FCSTD DOCUMENT  (FreeCAD 0.19R0.19.2)
Label: laptopStand015
License: All rights reserved
LicenseURL: http://en.wikipedia.org/wiki/All_rights_reserved
objects: Sketcher::SketchObject×1
note: 1 computed .brp shape members not serialized (recipe doc carries the construction recipe); baked Part::Feature solids carry a one-line shape summary decoded from their .brp

FEATURE [Sketcher::SketchObject] Sketch
  FullyConstrained = false
  sketch-geometry (54):
    g0: LineSegment StartX=-22.9272 StartY=136.221 StartZ=0 EndX=-22.9272 EndY=-103.779 EndZ=0
    g1: LineSegment StartX=-22.9272 StartY=136.221 StartZ=0 EndX=387.073 EndY=136.221 EndZ=0
    g2: LineSegment StartX=-22.9272 StartY=-103.779 StartZ=0 EndX=387.073 EndY=-103.779 EndZ=0
    g3: LineSegment StartX=387.073 StartY=136.221 StartZ=0 EndX=387.073 EndY=-103.779 EndZ=0
    g4: LineSegment StartX=-10.9272 StartY=124.221 StartZ=0 EndX=-10.9272 EndY=115.221 EndZ=0
    g5: LineSegment StartX=-10.9272 StartY=124.221 StartZ=0 EndX=-1.92719 EndY=124.221 EndZ=0
    g6: LineSegment StartX=-10.9272 StartY=-91.7794 StartZ=0 EndX=-10.9272 EndY=-82.7794 EndZ=0
    g7: LineSegment StartX=-10.9272 StartY=-91.7794 StartZ=0 EndX=-1.92719 EndY=-91.7794 EndZ=0
    g8: LineSegment StartX=375.073 StartY=-91.7794 StartZ=0 EndX=366.073 EndY=-91.7794 EndZ=0
    g9: LineSegment StartX=375.073 StartY=-91.7794 StartZ=0 EndX=375.073 EndY=-82.7794 EndZ=0
    g10: LineSegment StartX=375.073 StartY=115.221 StartZ=0 EndX=318.073 EndY=83.9235 EndZ=0
    g11: LineSegment StartX=-10.9272 StartY=-82.7794 StartZ=0 EndX=169.377 EndY=16.2206 EndZ=0
    g12: LineSegment StartX=-1.92719 StartY=124.221 StartZ=0 EndX=139.632 EndY=46.4944 EndZ=0
    g13: LineSegment StartX=366.073 StartY=-91.7794 StartZ=0 EndX=318.073 EndY=-65.424 EndZ=0
    g14: LineSegment StartX=366.073 StartY=124.221 StartZ=0 EndX=318.073 EndY=124.221 EndZ=0
    g15: LineSegment StartX=-10.9272 StartY=115.221 StartZ=0 EndX=-10.9272 EndY=-82.7794 EndZ=0
    g16: LineSegment StartX=-1.92719 StartY=-91.7794 StartZ=0 EndX=366.073 EndY=-91.7794 EndZ=0
    g17: LineSegment StartX=375.073 StartY=-82.7794 StartZ=0 EndX=375.073 EndY=115.221 EndZ=0
    g18: LineSegment StartX=-1.92719 StartY=124.221 StartZ=0 EndX=58.0728 EndY=124.221 EndZ=0
    g19: LineSegment StartX=-1.92719 StartY=-91.7794 StartZ=0 EndX=58.0728 EndY=-91.7794 EndZ=0
    g20: LineSegment StartX=306.073 StartY=-91.7794 StartZ=0 EndX=366.073 EndY=-91.7794 EndZ=0
    g21: LineSegment StartX=318.073 StartY=124.221 StartZ=0 EndX=366.073 EndY=124.221 EndZ=0
    g22: LineSegment StartX=58.0728 StartY=124.221 StartZ=0 EndX=46.0728 EndY=124.221 EndZ=0
    g23: LineSegment StartX=318.073 StartY=-91.7794 StartZ=0 EndX=306.073 EndY=-91.7794 EndZ=0
    g24: LineSegment StartX=58.0728 StartY=-91.7794 StartZ=0 EndX=46.0728 EndY=-91.7794 EndZ=0
    g25: LineSegment StartX=306.073 StartY=-81.8102 StartZ=0 EndX=224.513 EndY=-14.0532 EndZ=0
    g26: LineSegment StartX=46.0728 StartY=124.221 StartZ=0 EndX=139.632 EndY=46.4944 EndZ=0
    g27: LineSegment StartX=306.073 StartY=124.221 StartZ=0 EndX=189.124 EndY=27.0628 EndZ=0
    g28: LineSegment StartX=58.0728 StartY=-91.7794 StartZ=0 EndX=175.022 EndY=5.37834 EndZ=0
    g29: LineSegment StartX=46.0728 StartY=124.221 StartZ=0 EndX=46.0728 EndY=-91.7794 EndZ=0
    g30: LineSegment StartX=58.0728 StartY=-91.7794 StartZ=0 EndX=58.0728 EndY=124.221 EndZ=0
    g31: LineSegment StartX=318.073 StartY=124.221 StartZ=0 EndX=318.073 EndY=97.8651 EndZ=0
    g32: LineSegment StartX=306.073 StartY=114.251 StartZ=0 EndX=306.073 EndY=91.2763 EndZ=0
    g33: LineSegment StartX=182.073 StartY=23.1914 StartZ=0 EndX=189.124 EndY=27.0628 EndZ=0
    g34: LineSegment StartX=182.073 StartY=9.24976 StartZ=0 EndX=175.022 EndY=5.37834 EndZ=0
    g35: LineSegment StartX=224.513 StartY=46.4944 StartZ=0 EndX=306.073 EndY=114.251 EndZ=0
    g36: LineSegment StartX=175.022 StartY=27.0628 StartZ=0 EndX=58.0728 EndY=124.221 EndZ=0
    g37: LineSegment StartX=169.377 StartY=16.2206 StartZ=0 EndX=-10.9272 EndY=115.221 EndZ=0
    g38: LineSegment StartX=139.632 StartY=-14.0532 StartZ=0 EndX=46.0728 EndY=-91.7794 EndZ=0
    g39: LineSegment StartX=194.768 StartY=16.2206 StartZ=0 EndX=306.073 EndY=-44.8935 EndZ=0
    g40: LineSegment StartX=224.513 StartY=46.4944 StartZ=0 EndX=306.073 EndY=91.2763 EndZ=0
    g41: LineSegment StartX=175.022 StartY=27.0628 StartZ=0 EndX=182.073 EndY=23.1914 EndZ=0
    g42: LineSegment StartX=139.632 StartY=-14.0532 StartZ=0 EndX=-1.92719 EndY=-91.7794 EndZ=0
    g43: LineSegment StartX=189.124 StartY=5.37834 StartZ=0 EndX=182.073 EndY=9.24976 EndZ=0
    g44: LineSegment StartX=189.124 StartY=5.37834 StartZ=0 EndX=306.073 EndY=-91.7794 EndZ=0
    g45: LineSegment StartX=306.073 StartY=77.3346 StartZ=0 EndX=306.073 EndY=-44.8935 EndZ=0
    g46: LineSegment StartX=318.073 StartY=83.9235 StartZ=0 EndX=318.073 EndY=-51.4823 EndZ=0
    g47: LineSegment StartX=318.073 StartY=97.8651 StartZ=0 EndX=366.073 EndY=124.221 EndZ=0
    g48: LineSegment StartX=306.073 StartY=77.3346 StartZ=0 EndX=194.768 EndY=16.2206 EndZ=0
    g49: LineSegment StartX=306.073 StartY=-58.8351 StartZ=0 EndX=224.513 EndY=-14.0532 EndZ=0
    g50: LineSegment StartX=306.073 StartY=-58.8351 StartZ=0 EndX=306.073 EndY=-81.8102 EndZ=0
    g51: LineSegment StartX=318.073 StartY=-51.4823 StartZ=0 EndX=375.073 EndY=-82.7794 EndZ=0
    g52: LineSegment StartX=318.073 StartY=-65.424 StartZ=0 EndX=318.073 EndY=-91.7794 EndZ=0
    g53: LineSegment StartX=306.073 StartY=124.221 StartZ=0 EndX=-1.92719 EndY=124.221 EndZ=0
  constraints (102):
    c: Vertical(g0)
    c: Distance(g0) = 240
    c: Horizontal(g1)
    c: Distance(g1) = 410
    c: Coincident(g1,g0)
    c: Coincident(g2,g0)
    c: Horizontal(g2)
    c: Coincident(g3,g1)
    c: Vertical(g3)
    c: Coincident(g2,g3)
    c: Block(g1)
    c: Block(g4)
    c: Coincident(g5,g4)
    c: Block(g5)
    c: Block(g6)
    c: Coincident(g7,g6)
    c: Horizontal(g7)
    c: Distance(g7) = 9
    c: Block(g8)
    c: Coincident(g9,g8)
    c: Block(g9)
    c: Coincident(g42,g7)
    c: Coincident(g11,g6)
    c: Coincident(g12,g5)
    c: Coincident(g51,g9)
    c: Coincident(g13,g8)
    c: Coincident(g37,g4)
    c: Coincident(g53,g5)
    c: Coincident(g15,g4)
    c: Coincident(g15,g6)
    c: Coincident(g16,g7)
    c: Coincident(g16,g8)
    c: Coincident(g17,g9)
    c: Horizontal(g18)
    c: Distance(g18) = 60
    c: Horizontal(g19)
    c: Equal(g18,g19) = 60
    c: Horizontal(g20)
    c: Horizontal(g21)
    c: Coincident(g18,g5)
    c: Coincident(g19,g7)
    c: Distance(g20) = 60
    c: Coincident(g20,g8)
    c: Horizontal(g22)
    c: Distance(g22) = 12
    c: Horizontal(g23)
    c: Equal(g22,g23) = 12
    c: Horizontal(g24)
    c: Equal(g22,g24) = 12
    c: Coincident(g22,g18)
    c: Coincident(g23,g20)
    c: Coincident(g24,g19)
    c: Coincident(g36,g18)
    c: Coincident(g26,g22)
    c: Coincident(g44,g20)
    c: Coincident(g38,g24)
    c: Coincident(g28,g19)
    c: Coincident(g29,g22)
    c: Coincident(g29,g24)
    c: Coincident(g30,g19)
    c: Coincident(g30,g18)
    c: Coincident(g52,g23)
    c: PointOnObject(g48,g12)
    c: PointOnObject(g11,g13)
    c: Tangent(g11,g33)
    c: Coincident(g41,g33)
    c: Coincident(g43,g34)
    c: Tangent(g13,g37)
    c: PointOnObject(g37,g11)
    c: PointOnObject(g39,g10)
    c: Coincident(g33,g27)
    c: Tangent(g33,g40)
    c: Coincident(g12,g26)
    c: Coincident(g41,g36)
    c: Tangent(g12,g41)
    c: Coincident(g35,g40)
    c: Coincident(g34,g28)
    c: Coincident(g42,g38)
    c: Tangent(g34,g42)
    c: Coincident(g49,g25)
    c: Tangent(g13,g43)
    c: Coincident(g44,g43)
    c: Coincident(g35,g32)
    c: Tangent(g32,g45)
    c: Tangent(g31,g46)
    c: Coincident(g40,g32)
    c: Coincident(g47,g31)
    c: Tangent(g40,g47)
    c: Coincident(g10,g46)
    c: Coincident(g48,g45)
    c: Tangent(g10,g48)
    c: Coincident(g50,g25)
    c: Tangent(g13,g49)
    c: Coincident(g50,g49)
    c: Tangent(g45,g50)
    c: Coincident(g39,g45)
    c: Tangent(g39,g51)
    c: Coincident(g46,g51)
    c: Coincident(g52,g13)
    c: Tangent(g46,g52)
    c: Tangent(g14,g53)
    c: PointOnObject(g21,g14)
